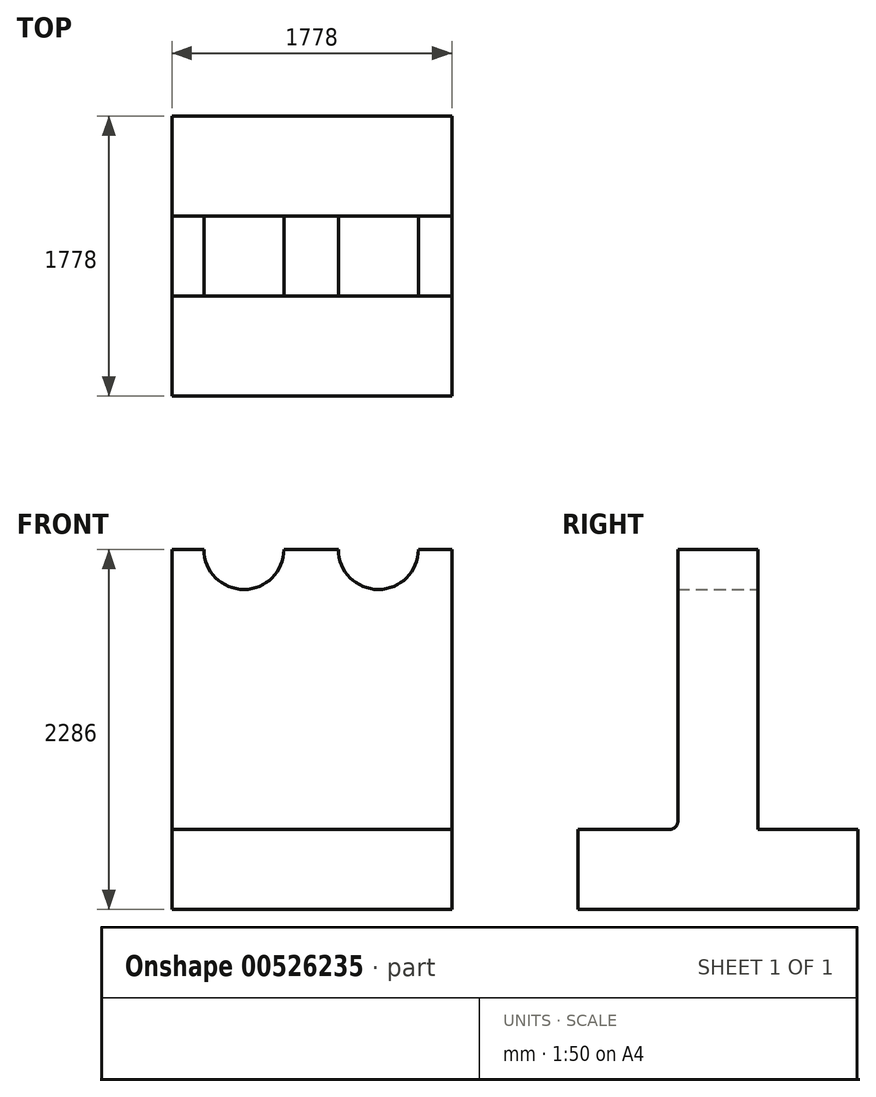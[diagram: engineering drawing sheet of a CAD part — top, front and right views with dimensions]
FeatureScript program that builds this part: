
annotation { "Feature Type Name" : "Feature", "Feature Type Description" : "" }
export const myFeature = defineFeature(function(context is Context, id is Id, definition is map)
    precondition{}
    {
        {
            var Q0;
            Q0=qCreatedBy(makeId("Right.planeOp"),FACE);
            var sketch = newSketch(context, id + "F0", { "sketchPlane" : qUnion([Q0])});
            skLineSegment(sketch, "E0.bottom", {"start": v(-884.33, -264) * mm, "end": v(893.67, -264) * mm});
            skLineSegment(sketch, "E0.top", {"start": v(-884.33, 244) * mm, "end": v(-249.33, 244) * mm});
            skLineSegment(sketch, "E0.left", {"start": v(-884.33, -264) * mm, "end": v(-884.33, 244) * mm});
            skLineSegment(sketch, "E0.right", {"start": v(893.67, -264) * mm, "end": v(893.67, 244) * mm});
            skLineSegment(sketch, "E1.bottom", {"start": v(-249.33, 2022) * mm, "end": v(258.67, 2022) * mm});
            skLineSegment(sketch, "E1.left", {"start": v(-249.33, 2022) * mm, "end": v(-249.33, 244) * mm});
            skLineSegment(sketch, "E1.right", {"start": v(258.67, 2022) * mm, "end": v(258.67, 244) * mm});
            skLineSegment(sketch, "E2.trimOffspring", {"start": v(258.67, 244) * mm, "end": v(893.67, 244) * mm});
            skSolve(sketch);
        }
        {
            var Q0;
            Q0 = qSketchRegion(id + "F0", true);
            extrude(context, id + "F1", {"entities" : qUnion([Q0]), "depth" : 1778 * mm, "offsetDistance" : 25.4 * mm});
        }
        {
            var Q0;
            Q0=makeQuery(id+"F1.opExtrude","SWEPT_FACE",FACE,{"disambiguationData":[OSD([sQuery(id+"F0.wireOp",EDGE,"E1.right")])]});
            var sketch = newSketch(context, id + "F2", { "sketchPlane" : qUnion([Q0])});
            skArc(sketch, "E3", {"start": v(-1565.48, 2022) * mm, "mid": v(-1311.48, 1768) * mm, "end": v(-1057.48, 2022) * mm});
            skArc(sketch, "E4", {"start": v(-711.42, 2022) * mm, "mid": v(-457.42, 1768) * mm, "end": v(-203.42, 2022) * mm});
            skLineSegment(sketch, "E5", {"start": v(-1565.48, 2022) * mm, "end": v(-203.42, 2022) * mm});
            skLineSegment(sketch, "E6", {"start": v(-203.42, 2022) * mm, "end": v(-1565.48, 2022) * mm});
            skLineSegment(sketch, "E7", {"start": v(-1057.48, 2022) * mm, "end": v(-711.42, 2022) * mm});
            skSolve(sketch);
        }
        {
            var Q0;
            Q0 = qSketchRegion(id + "F2", true);
            extrude(context, id + "F3", {"entities" : qUnion([Q0]), "operationType" : NewBodyOperationType.REMOVE, "endBound" : BoundingType.UP_TO_NEXT, "oppositeDirection" : true, "depth" : 25.4 * mm, "offsetDistance" : 25.4 * mm});
        }
        {
            var Q0;
            Q0=makeQuery(id+"F1.opExtrude","SWEPT_EDGE",EDGE,{"disambiguationData":[OSD([sQuery(id+"F0.wireOp",EDGE,"E0.top"),sQuery(id+"F0.wireOp",EDGE,"E1.left")])]});
            fillet(context, id + "F4", {"entities" : qUnion([Q0]), "radius" : 50.8 * mm, "tangentPropagation" : true, "allowEdgeOverflow" : false});
        }
    });
